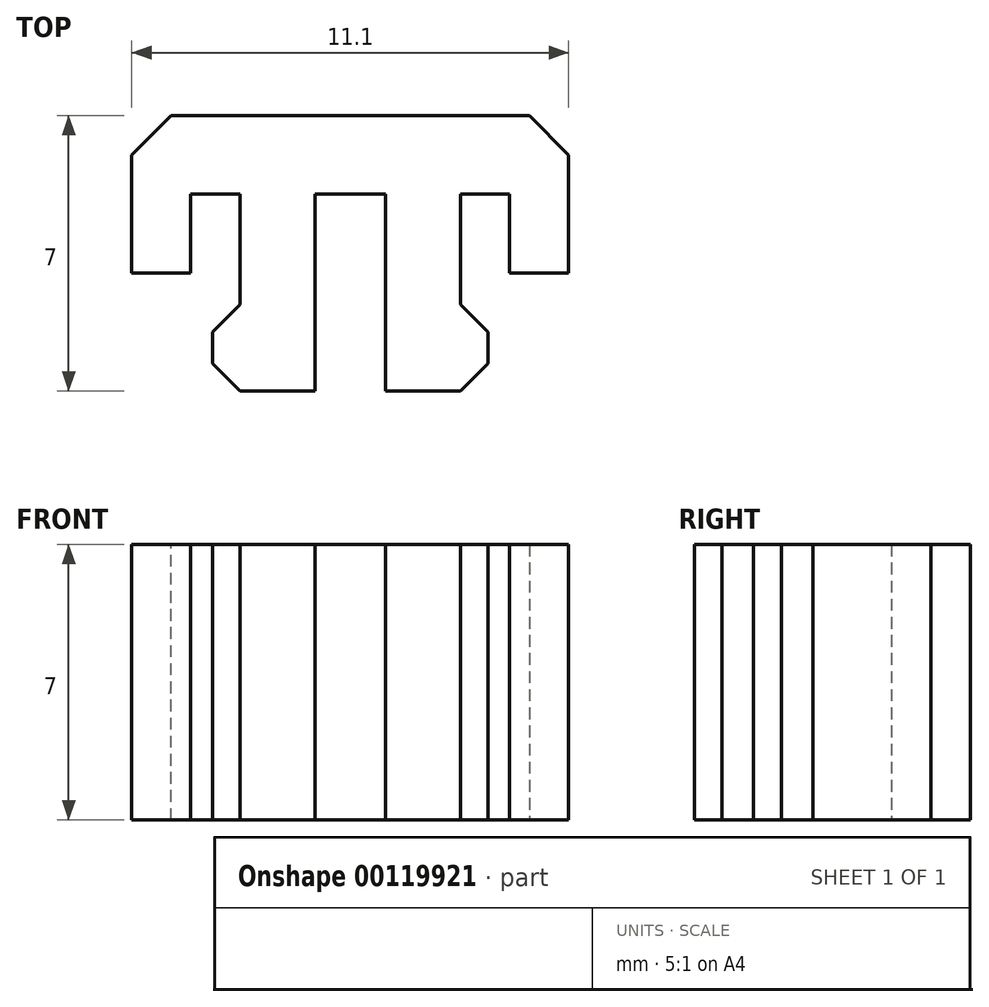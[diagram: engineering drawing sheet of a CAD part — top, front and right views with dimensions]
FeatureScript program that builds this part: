
annotation { "Feature Type Name" : "Feature", "Feature Type Description" : "" }
export const myFeature = defineFeature(function(context is Context, id is Id, definition is map)
    precondition{}
    {
        {
            var Q0;
            Q0=qCreatedBy(makeId("Top.planeOp"),FACE);
            var sketch = newSketch(context, id + "F0", { "sketchPlane" : qUnion([Q0])});
            skLineSegment(sketch, "E0.bottom", {"start": v(-0.9, 0) * mm, "end": v(-2.8, 0) * mm});
            skLineSegment(sketch, "E0.top", {"start": v(-0.9, -5) * mm, "end": v(-2.8, -5) * mm});
            skLineSegment(sketch, "E0.left", {"start": v(-0.9, 0) * mm, "end": v(-0.9, -5) * mm});
            skLineSegment(sketch, "E0.right", {"start": v(-2.8, 0) * mm, "end": v(-2.8, -5) * mm});
            skLineSegment(sketch, "E1", {"start": v(-2.8, -5) * mm, "end": v(-3.5, -4.3) * mm});
            skLineSegment(sketch, "E2", {"start": v(-3.5, -4.3) * mm, "end": v(-3.5, -3.5) * mm});
            skLineSegment(sketch, "E3", {"start": v(-3.5, -3.5) * mm, "end": v(-2.8, -2.8) * mm});
            skLineSegment(sketch, "E4", {"start": v(-2.8, 0) * mm, "end": v(-4.05, 0) * mm});
            skLineSegment(sketch, "E5", {"start": v(-4.05, 0) * mm, "end": v(-4.05, -2) * mm});
            skLineSegment(sketch, "E6", {"start": v(-4.05, -2) * mm, "end": v(-5.55, -2) * mm});
            skLineSegment(sketch, "E7", {"start": v(-5.55, -2) * mm, "end": v(-5.55, 2) * mm});
            skLineSegment(sketch, "E8", {"start": v(-5.55, 2) * mm, "end": v(0, 2) * mm});
            skLineSegment(sketch, "E9.MirrorCS", {"start": v(2.8, 0) * mm, "end": v(2.8, -5) * mm});
            skLineSegment(sketch, "E10.MirrorCS", {"start": v(0.9, 0) * mm, "end": v(0.9, -5) * mm});
            skLineSegment(sketch, "E11.MirrorCS", {"start": v(0.9, 0) * mm, "end": v(2.8, 0) * mm});
            skLineSegment(sketch, "E12.MirrorCS", {"start": v(5.55, -2) * mm, "end": v(5.55, 2) * mm});
            skLineSegment(sketch, "E13.MirrorCS", {"start": v(3.5, -3.5) * mm, "end": v(2.8, -2.8) * mm});
            skLineSegment(sketch, "E14.MirrorCS", {"start": v(0.9, -5) * mm, "end": v(2.8, -5) * mm});
            skLineSegment(sketch, "E15.MirrorCS", {"start": v(5.55, 2) * mm, "end": v(0, 2) * mm});
            skLineSegment(sketch, "E16.MirrorCS", {"start": v(2.8, -5) * mm, "end": v(3.5, -4.3) * mm});
            skLineSegment(sketch, "E17.MirrorCS", {"start": v(2.8, 0) * mm, "end": v(4.05, 0) * mm});
            skLineSegment(sketch, "E18.MirrorCS", {"start": v(3.5, -4.3) * mm, "end": v(3.5, -3.5) * mm});
            skLineSegment(sketch, "E19.MirrorCS", {"start": v(4.05, -2) * mm, "end": v(5.55, -2) * mm});
            skLineSegment(sketch, "E20.MirrorCS", {"start": v(4.05, 0) * mm, "end": v(4.05, -2) * mm});
            skLineSegment(sketch, "E21", {"start": v(-0.9, 0) * mm, "end": v(0.9, 0) * mm});
            skSolve(sketch);
        }
        {
            var Q0;
            Q0=qSketchRegion(id+"F0",true);
            extrude(context, id + "F1", {"entities" : qUnion([Q0]), "depth" : 7 * mm});
        }
        {
            var Q0;
            Q0=makeQuery(id+"F1.opExtrude","SWEPT_EDGE",EDGE,{"disambiguationData":[OSD([sQuery(id+"F0.wireOp",EDGE,"E7"),sQuery(id+"F0.wireOp",EDGE,"E8")])]});
            var Q1;
            Q1=makeQuery(id+"F1.opExtrude","SWEPT_EDGE",EDGE,{"disambiguationData":[OSD([sQuery(id+"F0.wireOp",EDGE,"E12.MirrorCS"),sQuery(id+"F0.wireOp",EDGE,"E15.MirrorCS")])]});
            chamfer(context, id + "F2", {"entities" : qUnion([Q0, Q1]), "width" : 1 * mm, "tangentPropagation" : true});
        }
    });
